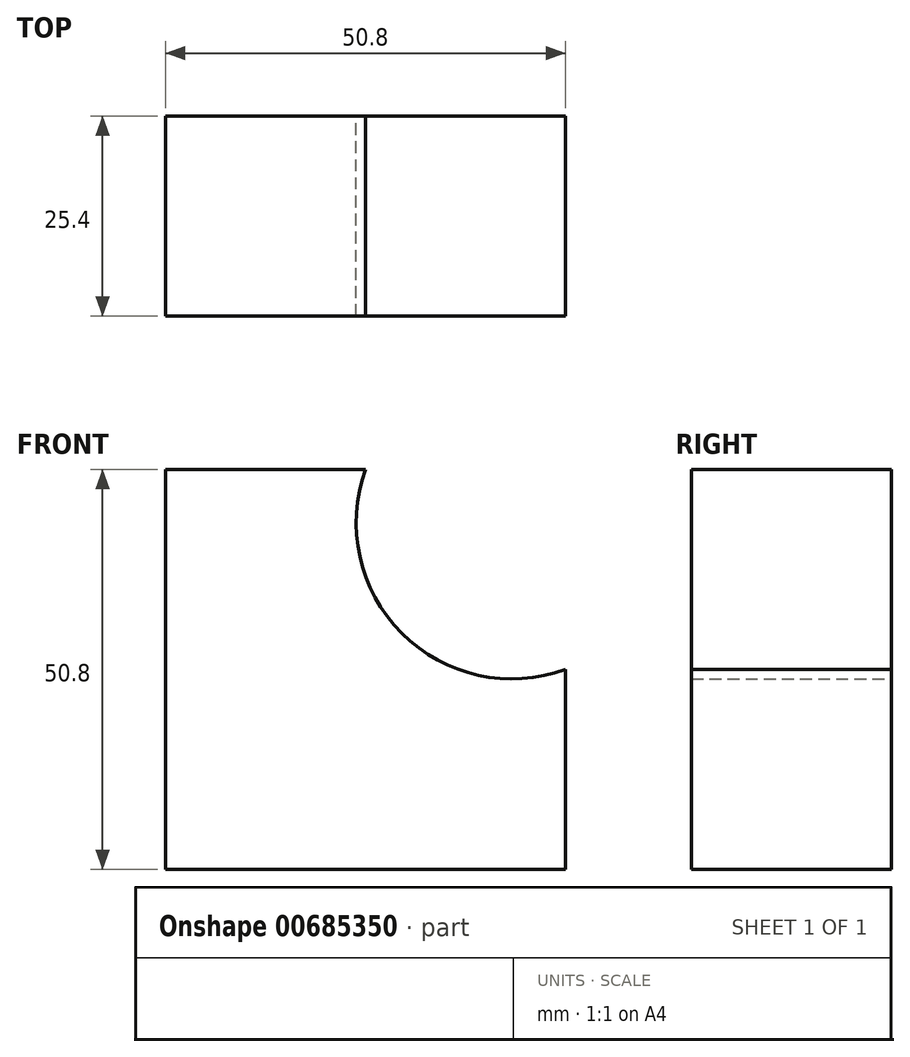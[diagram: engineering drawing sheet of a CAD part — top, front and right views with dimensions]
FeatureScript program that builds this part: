
annotation { "Feature Type Name" : "Feature", "Feature Type Description" : "" }
export const myFeature = defineFeature(function(context is Context, id is Id, definition is map)
    precondition{}
    {
        {
            var Q0;
            Q0=qCreatedBy(makeId("Front.planeOp"),FACE);
            var sketch = newSketch(context, id + "F0", { "sketchPlane" : qUnion([Q0])});
            skLineSegment(sketch, "E0", {"start": v(0, 0) * mm, "end": v(0, -50.8) * mm});
            skLineSegment(sketch, "E1", {"start": v(0, -50.8) * mm, "end": v(50.8, -50.8) * mm});
            skLineSegment(sketch, "E2", {"start": v(50.8, -50.8) * mm, "end": v(50.8, -25.4) * mm});
            skLineSegment(sketch, "E3", {"start": v(0, 0) * mm, "end": v(25.4, 0) * mm});
            skArc(sketch, "E4", {"start": v(25.4, 0) * mm, "mid": v(30, -20.8) * mm, "end": v(50.8, -25.4) * mm});
            skSolve(sketch);
        }
        {
            var Q0;
            Q0=makeQuery(id+"F0.imprint","IMPRINT",FACE,{"disambiguationData":[TD([[makeQuery(id+"F0.imprint","IMPRINT",EDGE,{"derivedFrom":sQuery(id+"F0.wireOp",EDGE,"E0")}),1.0]])]});
            extrude(context, id + "F1", {"entities" : qUnion([Q0]), "depth" : 25.4 * mm, "offsetDistance" : 25.4 * mm});
        }
    });
